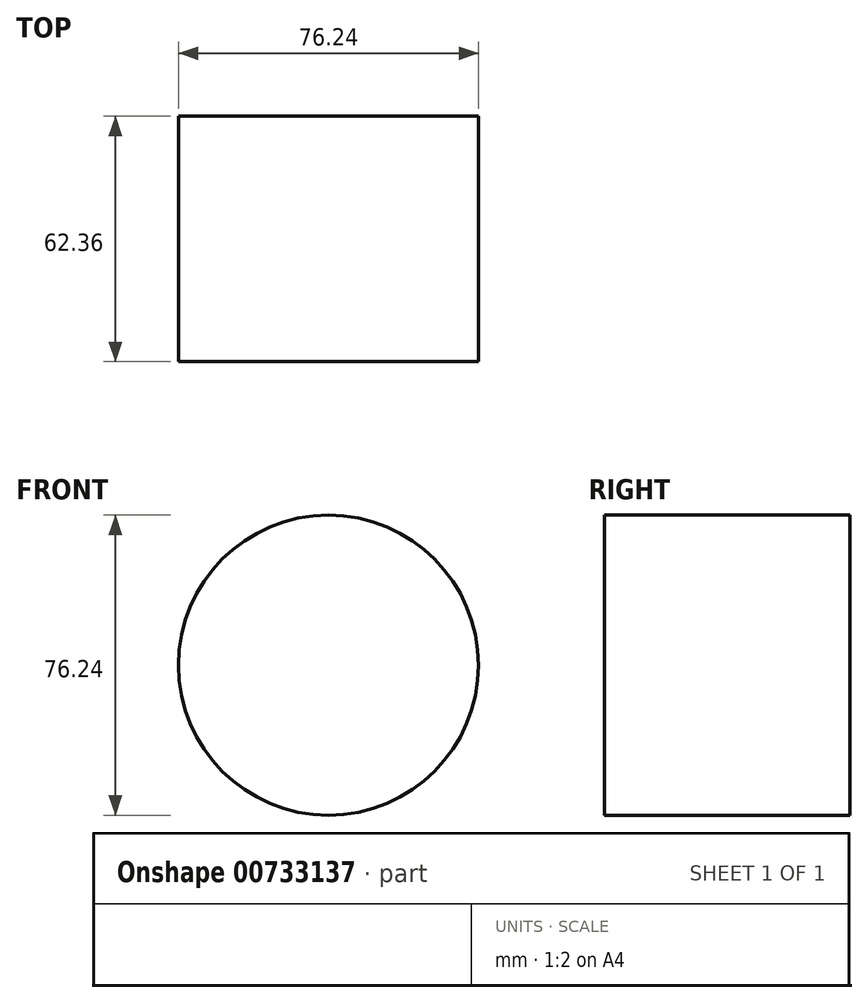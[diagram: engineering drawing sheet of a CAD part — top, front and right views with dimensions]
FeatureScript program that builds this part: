
annotation { "Feature Type Name" : "Feature", "Feature Type Description" : "" }
export const myFeature = defineFeature(function(context is Context, id is Id, definition is map)
    precondition{}
    {
        {
            var Q0;
            Q0=qCreatedBy(makeId("Front.planeOp"),FACE);
            var sketch = newSketch(context, id + "F0", { "sketchPlane" : qUnion([Q0])});
            skCircle(sketch, "E0", {"center": v(-38.12, 0) * mm, "radius": 38.12 * mm});
            skSolve(sketch);
        }
        {
            var Q0;
            Q0=makeQuery(id+"F0.imprint","IMPRINT",FACE,{"disambiguationData":[TD([[makeQuery(id+"F0.imprint","IMPRINT",EDGE,{"derivedFrom":sQuery(id+"F0.wireOp",EDGE,"E0")}),1.0]])]});
            var sketch = newSketch(context, id + "F1", { "sketchPlane" : qUnion([Q0])});
            skSolve(sketch);
        }
        {
            var Q0;
            Q0=makeQuery(id+"F1.imprint","IMPRINT",FACE,{"disambiguationData":[TD([[makeQuery(id+"F1.imprint","IMPRINT",EDGE,{"derivedFrom":makeQuery(id+"F0.imprint","IMPRINT",EDGE,{"derivedFrom":sQuery(id+"F0.wireOp",EDGE,"E0")})}),1.0]])]});
            extrude(context, id + "F2", {"entities" : qUnion([Q0]), "depth" : 62.36 * mm, "offsetDistance" : 25.4 * mm});
        }
    });
